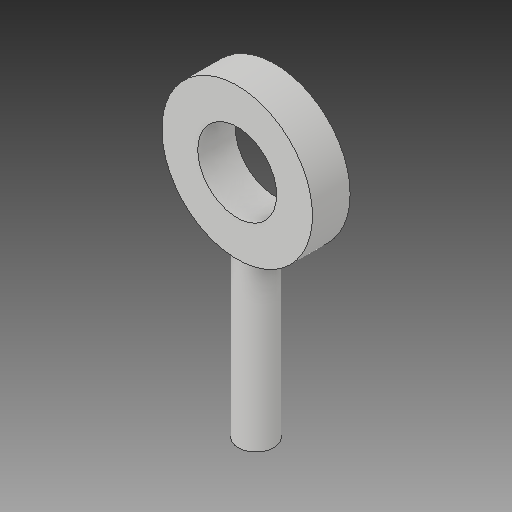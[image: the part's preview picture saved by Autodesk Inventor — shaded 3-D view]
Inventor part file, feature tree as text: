
AUTODESK INVENTOR PART (.ipt)
format: ipt  version: 2018 (Build 220112000, 112)  size: 114,688 bytes
history: native  units: in
note: dims shown in document units (in); Inventor stores cm internally (conversion verified against a paired STEP export)
features: plane x2, extrude x2, sketch x2
ambient origin geometry x8: Origin, YZ Plane, XZ Plane, XY Plane, X Axis, Y Axis, Z Axis, Center Point
bodies: Solid1 (feature_tree)
feature tree (6):
  plane  "Work Plane1"
  extrude  "Extrusion1"  Depth=0.68in
  plane  "Work Plane2"
  extrude  "Extrusion2"  Depth=0.74in
  sketch  "Sketch2"  dims[d1=0.2565in d2=0.68in]
  sketch  "Sketch3"  dims[d3=0.162in d4=0.74in d5=0.17in d6=0.0in d7=-0.339in d8=0.162in d9=0.74in d10=0.0in]
